# Revit family: HC_Boiler_MEPcontent_De Dietrich Thermique_Thermodynamic water heater TWH  EH
name_source: partatom
category: Mechanical Equipment
revit_build: Autodesk Revit MEP 2015 (Build: 20151007_1515(x64)
units: mm (PartAtom-declared; Revit-internal decimal feet)

## types (1)
- 300 EH
    Article Description = Water heater with heat pump
    Article Type = 300 EH
    Black = Color RGB 045-045-045
    Blue = Color RGB 002-061-157
    Content Supplier URL = www.mepcontent.eu
    Custom = No
    Description = Water heater with heat pump
    Diameter = 600 mm
    Domestic Cold Water Diameter = 19 mm  [stored 0.062336 ft]
    Domestic Hot Water Diameter = 19 mm  [stored 0.062336 ft]
    Drain Diameter = 16 mm  [stored 0.0524934 ft]
    EMCS Version = 3.0
    ETIM Article Class = EC011396
    Exhaust Air Diameter = 200 mm  [stored 0.656168 ft]
    Family Version = 10.24
    GTIN = 3661238496897
    Glass = Color RGB 218-227-224
    Green = Color RGB 106-158-058
    Grey = Color RAL 9006
    Height = 2000 mm  [stored 6.56168 ft]
    Hydronic Return Diameter = 19 mm  [stored 0.062336 ft]
    Hydronic Supply Diameter = 19 mm  [stored 0.062336 ft]
    IFCExportAs = IfcBoilerType
    Length = 690 mm  [stored 2.26378 ft]
    MEPcontent Class = BOILER
    Manufacturer = De Dietrich Thermique
    Manufacturer Art. No. = 100017411
    Manufacturer URL = http://www.dedietrich-thermique.fr
    Model = 300 EH
    Power = 500 W
    Product Line = De Dietrich Thermique
    Red = Color RGB 198-000-000
    Revit Version = 2015
    Supply Air Diameter = 200 mm  [stored 0.656168 ft]
    URL = www.stabiplan.com
    Use Nominal Diameter = Yes
    Voltage = 230 V
    Volume = 260.0 L
    White = Color RAL 9016

note: [stored X ft] marks values corroborated as IEEE doubles in the binary element streams (Revit-internal decimal feet)

## geometry (parser evidence)
native form markers: Sweep x4
no freeform markers — native parametric forms only
